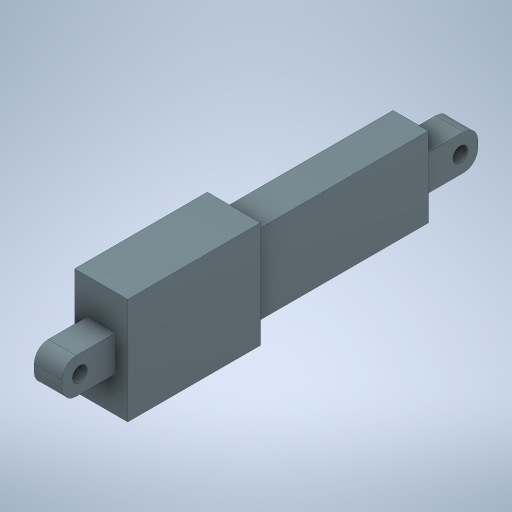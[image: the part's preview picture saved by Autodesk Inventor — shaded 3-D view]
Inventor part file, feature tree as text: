
AUTODESK INVENTOR PART (.ipt)
format: ipt  version: 2024 (Build 280153000, 153)  size: 313,856 bytes
history: native  units: mm
features: extrude x5, sketch x5, other x2, mirror x2, fillet x1
ambient origin geometry x8: Origin, YZ Plane, XZ Plane, XY Plane, X Axis, Y Axis, Z Axis, Center Point
bodies: Body1 (feature_tree)
feature tree (15):
  other  "솔리드1"
  extrude  "돌출1"  Depth=15.0mm
  extrude  "돌출2"  Depth=30.0mm
  extrude  "돌출3"  Depth=15.0mm
  extrude  "돌출4"  Depth=7.5mm
  extrude  "돌출5"  Depth=37.5mm TaperAngle=0.0deg
  other  "작업 평면1"
  mirror  "미러1"
  mirror  "미러2"
  fillet  "모깎기1"  Radius=10.0mm
  sketch  "스케치1"
  sketch  "스케치2"
  sketch  "스케치3"
  sketch  "스케치4"
  sketch  "스케치5"
